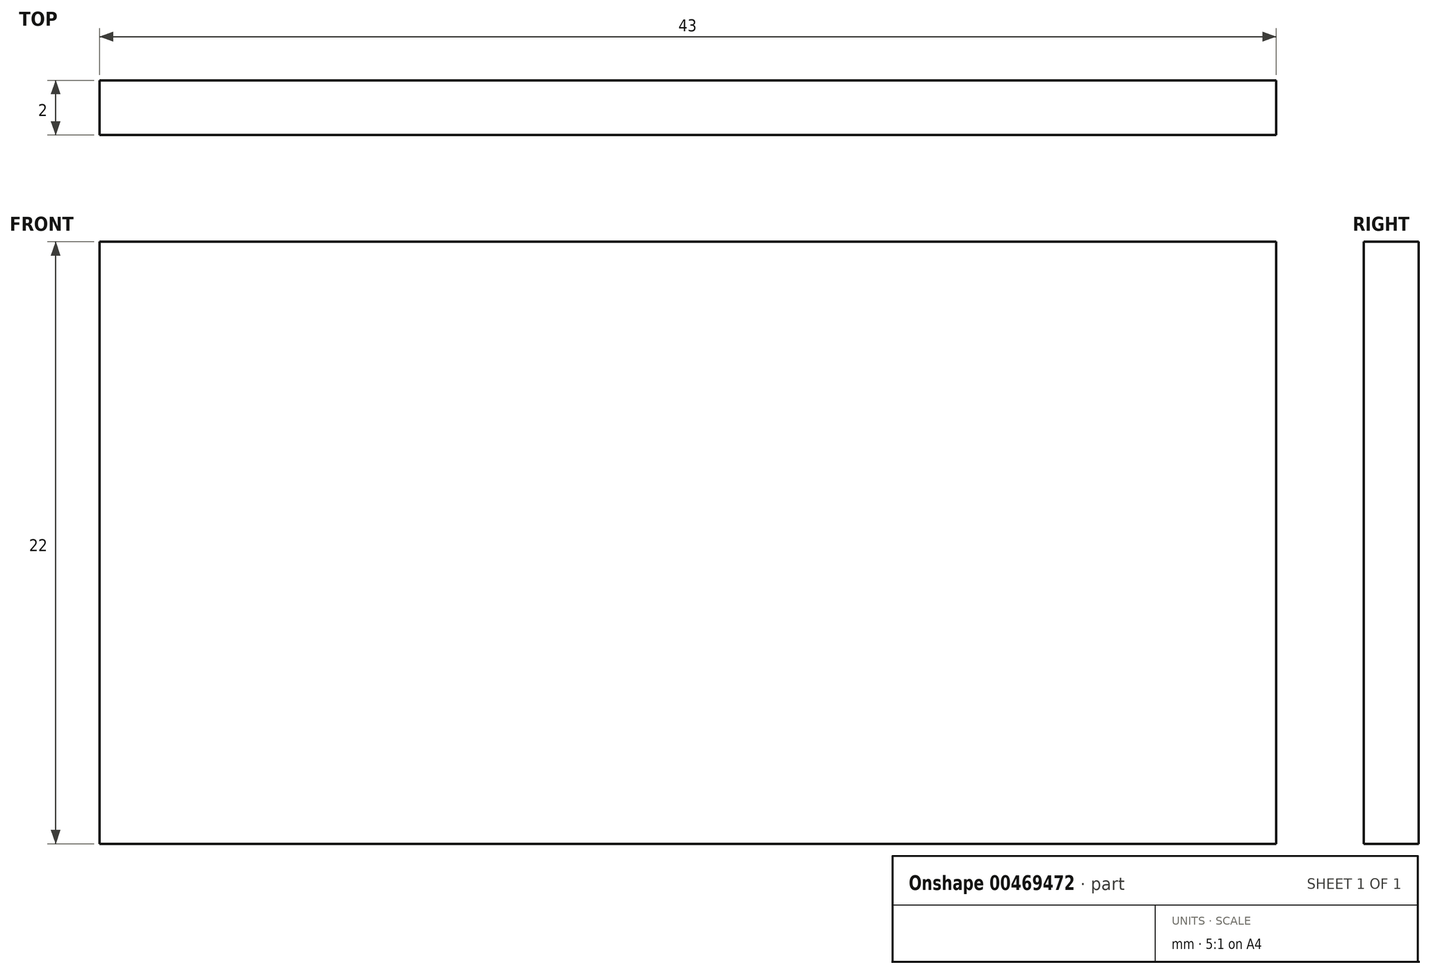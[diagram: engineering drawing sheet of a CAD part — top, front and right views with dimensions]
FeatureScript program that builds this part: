
annotation { "Feature Type Name" : "Feature", "Feature Type Description" : "" }
export const myFeature = defineFeature(function(context is Context, id is Id, definition is map)
    precondition{}
    {
        {
            var Q0;
            Q0=qCreatedBy(makeId("Front.planeOp"),FACE);
            var sketch = newSketch(context, id + "F0", { "sketchPlane" : qUnion([Q0])});
            skLineSegment(sketch, "E0.bottom", {"start": v(0, 0) * mm, "end": v(43, 0) * mm});
            skLineSegment(sketch, "E0.top", {"start": v(0, 22) * mm, "end": v(43, 22) * mm});
            skLineSegment(sketch, "E0.left", {"start": v(0, 0) * mm, "end": v(0, 22) * mm});
            skLineSegment(sketch, "E0.right", {"start": v(43, 0) * mm, "end": v(43, 22) * mm});
            skSolve(sketch);
        }
        {
            var Q0;
            Q0=makeQuery(id+"F0.imprint","IMPRINT",FACE,{"disambiguationData":[TD([[makeQuery(id+"F0.imprint","IMPRINT",EDGE,{"derivedFrom":sQuery(id+"F0.wireOp",EDGE,"E0.bottom")}),1.0]])]});
            extrude(context, id + "F1", {"entities" : qUnion([Q0]), "depth" : 2 * mm});
        }
    });
